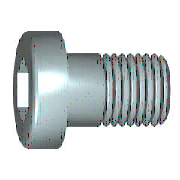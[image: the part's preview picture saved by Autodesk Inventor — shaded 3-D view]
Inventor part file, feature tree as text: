
AUTODESK INVENTOR PART (.ipt)
format: ipt  version: 2020 (Build 240168000, 168)  size: 185,856 bytes
history: native  units: mm (DEFAULTED — no unit token found)
features: sketch x2, chamfer x1, extrude x1, other x1, plane x1
ambient origin geometry x7: Origin, YZ Plane, XY Plane, X Axis, Y Axis, Z Axis, Center Point
bodies: Solid1 (feature_tree), Body (feature_tree)
feature tree (6):
  sketch  "Sketch1"  dims[d0=2.8mm]
  chamfer  "Chamfer2"  Angle=60.0deg  [1 undecoded]
  extrude  "Slot"  Depth=2.0mm
  other  "Work Axis1"
  plane  "Work Plane1"
  sketch  "Sketch2"  dims[d1=1.6mm d2=60.0deg d3=4.0mm d4=3.464102mm d5=7.0mm d10=90.0deg d11=10.0mm d6=0.0mm d7=14.0mm d8=0.0mm d9=0.429415mm d12=0.429415mm d14=0.0mm d15=3.3mm d16=2.0mm d17=35.0mm d28=45.0deg d30=0.0mm d31=0.0mm d32=45.0deg d33=0.4mm d34=90.0deg]
note: 1 required parameter value undecoded (feature->parameter linkage not recoverable at this tier; creation-order binding heuristic only, values carry confidence <= 0.55)
